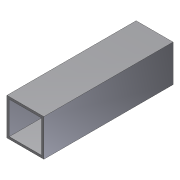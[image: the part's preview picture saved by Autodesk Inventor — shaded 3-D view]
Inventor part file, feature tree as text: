
AUTODESK INVENTOR PART (.ipt)
format: ipt  version: 2012 (Build 160160000, 160)  size: 76,288 bytes
history: native  units: in
note: dims shown in document units (in); Inventor stores cm internally (conversion verified against a paired STEP export)
features: extrude x1, shell x1, sketch x1
ambient origin geometry x8: Origin, YZ Plane, XZ Plane, XY Plane, X Axis, Y Axis, Z Axis, Center Point
bodies: Solid1 (feature_tree)
feature tree (3):
  extrude  "Extrusion1"  Depth=1.0in
  shell  "Shell1"  Thickness=3.5in
  sketch  "Sketch1"  dims[d0=1.0in d1=1.0in d2=3.5in d3=0.0in d4=0.0625in]
